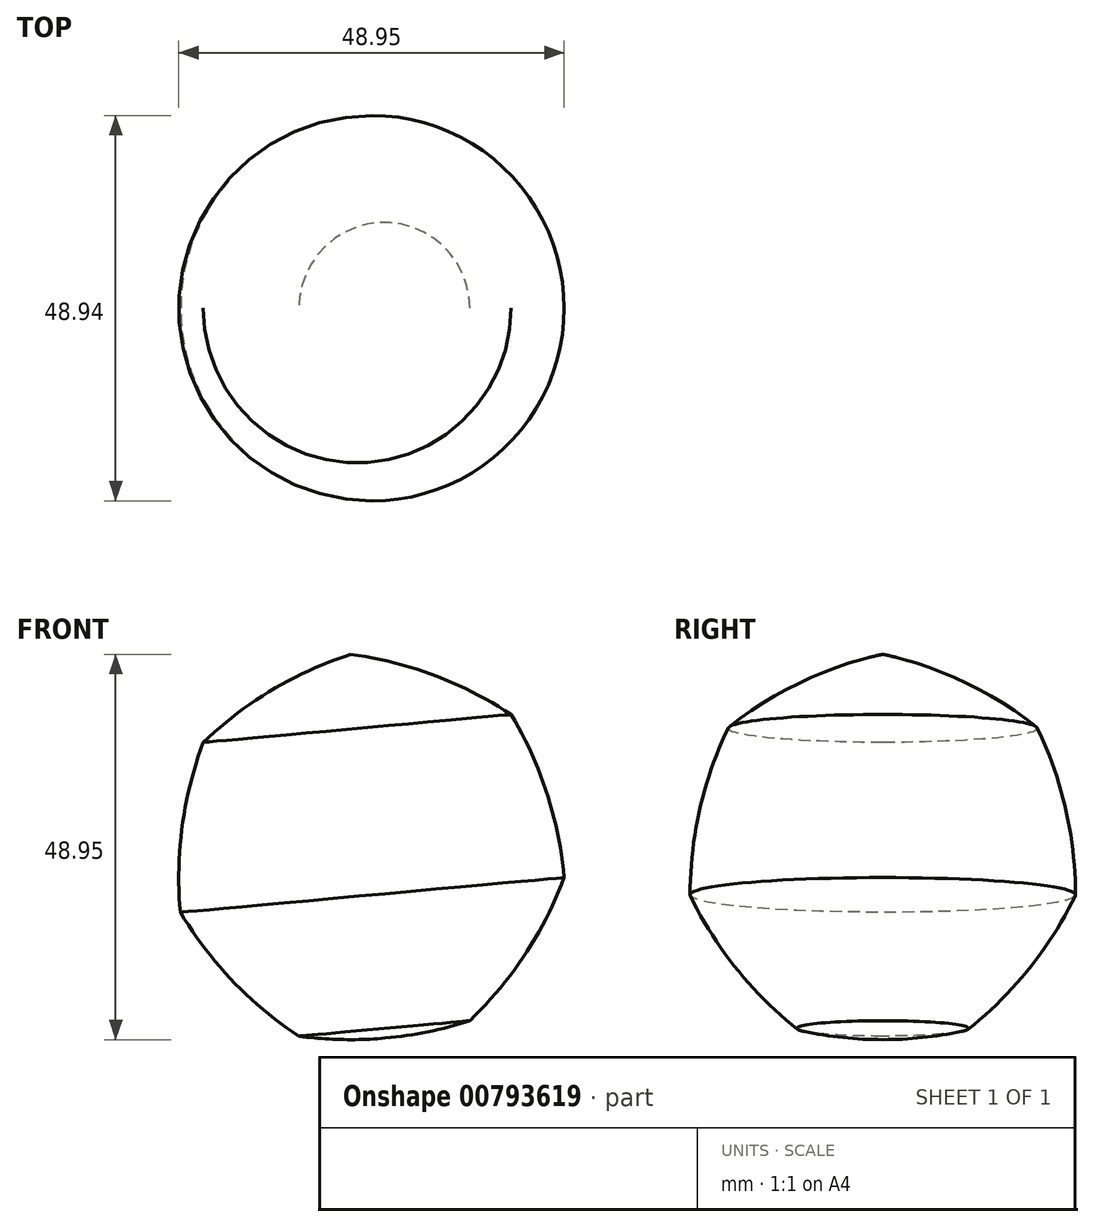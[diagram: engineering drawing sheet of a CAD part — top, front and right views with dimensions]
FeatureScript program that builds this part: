
annotation { "Feature Type Name" : "Feature", "Feature Type Description" : "" }
export const myFeature = defineFeature(function(context is Context, id is Id, definition is map)
    precondition{}
    {
        {
            var Q0;
            Q0=qCreatedBy(makeId("Front.planeOp"),FACE);
            var sketch = newSketch(context, id + "F0", { "sketchPlane" : qUnion([Q0])});
            skArc(sketch, "E0", {"start": v(-23.87, -7.77) * mm, "mid": v(-17.23, -16.49) * mm, "end": v(-8.8, -23.5) * mm});
            skArc(sketch, "E1", {"start": v(-20.96, 13.82) * mm, "mid": v(-23.63, 3.19) * mm, "end": v(-23.87, -7.77) * mm});
            skArc(sketch, "E2.trimOffspring", {"start": v(-2.26, 25) * mm, "mid": v(-12.24, 20.46) * mm, "end": v(-20.96, 13.82) * mm});
            skArc(sketch, "E3.trimOffspring", {"start": v(18.13, 17.36) * mm, "mid": v(8.37, 22.33) * mm, "end": v(-2.26, 25) * mm});
            skArc(sketch, "E4.trimOffspring", {"start": v(24.88, -3.36) * mm, "mid": v(22.67, 7.38) * mm, "end": v(18.13, 17.36) * mm});
            skArc(sketch, "E5.trimOffspring", {"start": v(12.89, -21.54) * mm, "mid": v(19.9, -13.12) * mm, "end": v(24.88, -3.36) * mm});
            skArc(sketch, "E6.trimOffspring", {"start": v(-8.8, -23.5) * mm, "mid": v(2.15, -23.75) * mm, "end": v(12.89, -21.54) * mm});
            skLineSegment(sketch, "E7", {"start": v(-2.26, 25) * mm, "end": v(2.15, -23.75) * mm});
            skSolve(sketch);
        }
        {
            var Q0;
            {var subQ1=sQuery(id+"F0.wireOp",EDGE,"E0");Q0=makeQuery(id+"F0.imprint","IMPRINT",FACE,{"disambiguationData":[TD([[makeQuery(id+"F0.imprint","IMPRINT",EDGE,{"derivedFrom":subQ1}),1.0]])]});}
            var Q1;
            Q1=sQuery(id+"F0.wireOp",EDGE,"E7");
            revolve(context, id + "F1", {"surfaceOperationType" : NewSurfaceOperationType.NEW, "entities" : qUnion([Q0]), "axis" : qUnion([Q1]), "revolveType" : RevolveType.FULL});
        }
    });
